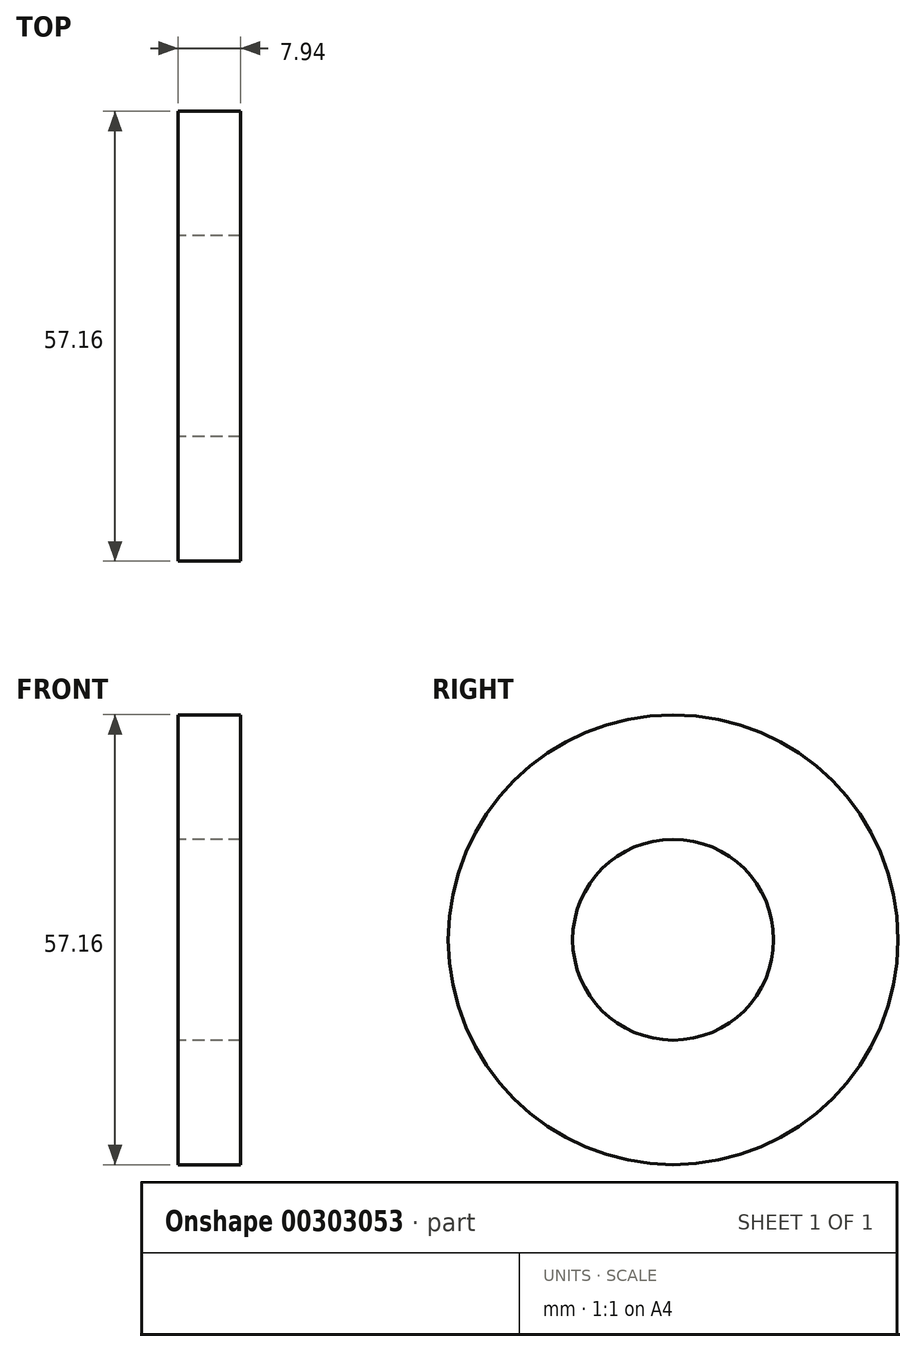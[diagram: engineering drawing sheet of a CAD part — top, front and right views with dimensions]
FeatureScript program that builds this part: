
annotation { "Feature Type Name" : "Feature", "Feature Type Description" : "" }
export const myFeature = defineFeature(function(context is Context, id is Id, definition is map)
    precondition{}
    {
        {
            var Q0;
            Q0=qCreatedBy(makeId("Right.planeOp"),FACE);
            var sketch = newSketch(context, id + "F0", { "sketchPlane" : qUnion([Q0])});
            skCircle(sketch, "E0", {"center": v(0, 0) * mm, "radius": 28.58 * mm});
            skCircle(sketch, "E1", {"center": v(0, 0) * mm, "radius": 12.76 * mm});
            skSolve(sketch);
        }
        {
            var Q0;
            Q0=makeQuery(id+"F0.imprint","IMPRINT",FACE,{"disambiguationData":[TD([[makeQuery(id+"F0.imprint","IMPRINT",EDGE,{"derivedFrom":sQuery(id+"F0.wireOp",EDGE,"E0")}),1.0]])]});
            extrude(context, id + "F1", {"entities" : qUnion([Q0]), "depth" : 7.94 * mm, "symmetric" : true});
        }
    });
